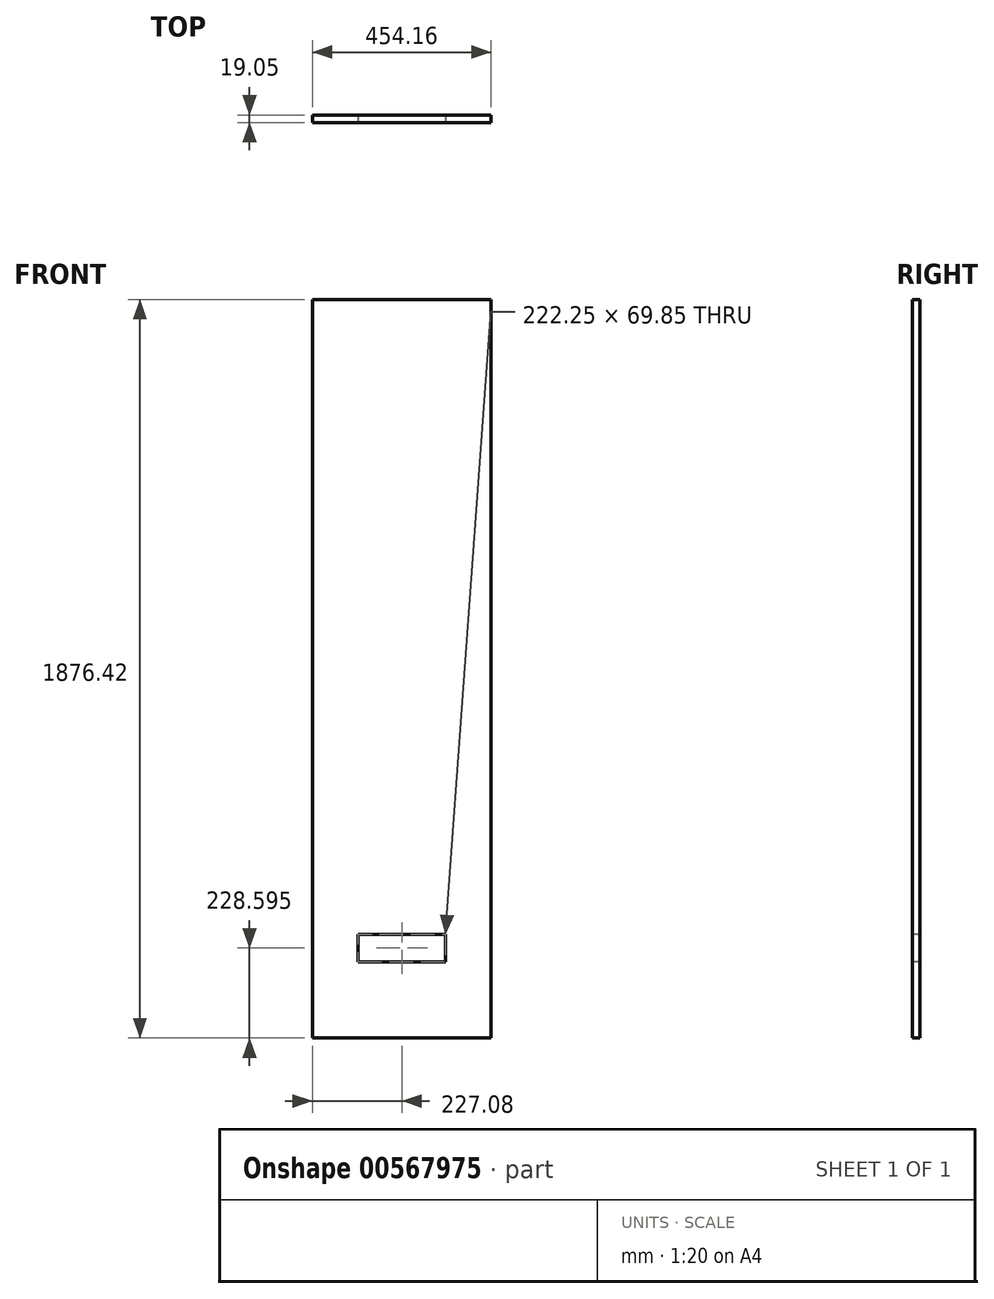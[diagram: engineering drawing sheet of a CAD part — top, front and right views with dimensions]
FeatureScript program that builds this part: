
annotation { "Feature Type Name" : "Feature", "Feature Type Description" : "" }
export const myFeature = defineFeature(function(context is Context, id is Id, definition is map)
    precondition{}
    {
        {
            var Q0;
            Q0=qCreatedBy(makeId("Front.planeOp"),FACE);
            var sketch = newSketch(context, id + "F0", { "sketchPlane" : qUnion([Q0])});
            skLineSegment(sketch, "E0.bottom", {"start": v(227.08, 965.2) * mm, "end": v(-227.08, 965.2) * mm});
            skLineSegment(sketch, "E0.top", {"start": v(227.08, -965.2) * mm, "end": v(-227.08, -965.2) * mm});
            skLineSegment(sketch, "E0.left", {"start": v(227.08, 965.2) * mm, "end": v(227.08, -965.2) * mm});
            skLineSegment(sketch, "E0.right", {"start": v(-227.08, 965.2) * mm, "end": v(-227.08, -965.2) * mm});
            skPoint(sketch, "E0.middle", {"position": v(0, 0) * mm});
            skSolve(sketch);
        }
        {
            var Q0;
            Q0=makeQuery(id+"F0.imprint","IMPRINT",FACE,{"disambiguationData":[TD([[makeQuery(id+"F0.imprint","IMPRINT",EDGE,{"derivedFrom":sQuery(id+"F0.wireOp",EDGE,"E0.bottom")}),1.0]])]});
            extrude(context, id + "F1", {"entities" : qUnion([Q0]), "depth" : 19.05 * mm, "offsetDistance" : 25.4 * mm});
        }
        {
            var Q0;
            Q0=makeQuery(id+"F1.opExtrude","SWEPT_FACE",FACE,{"disambiguationData":[OSD([sQuery(id+"F0.wireOp",EDGE,"E0.top")])]});
            extrude(context, id + "F2", {"entities" : qUnion([Q0]), "operationType" : NewBodyOperationType.REMOVE, "oppositeDirection" : true, "depth" : 53.97 * mm, "offsetDistance" : 25.4 * mm});
        }
        {
            var Q0;
            Q0=makeQuery(id+"F1.opExtrude","CAP_FACE",FACE,{"disambiguationData":[OSD([sQuery(id+"F0.wireOp",EDGE,"E0.bottom"),sQuery(id+"F0.wireOp",EDGE,"E0.top"),sQuery(id+"F0.wireOp",EDGE,"E0.left"),sQuery(id+"F0.wireOp",EDGE,"E0.right")])],"isStart":false});
            var sketch = newSketch(context, id + "F3", { "sketchPlane" : qUnion([Q0])});
            skLineSegment(sketch, "E1", {"start": v(0, -911.22) * mm, "end": v(0, -682.62) * mm});
            skLineSegment(sketch, "E2.bottom", {"start": v(111.13, -647.7) * mm, "end": v(-111.12, -647.7) * mm});
            skLineSegment(sketch, "E2.top", {"start": v(111.13, -717.55) * mm, "end": v(-111.13, -717.55) * mm});
            skLineSegment(sketch, "E2.left", {"start": v(111.13, -647.7) * mm, "end": v(111.13, -717.55) * mm});
            skLineSegment(sketch, "E2.right", {"start": v(-111.12, -647.7) * mm, "end": v(-111.13, -717.55) * mm});
            skPoint(sketch, "E2.middle", {"position": v(0, -682.62) * mm});
            skSolve(sketch);
        }
        {
            var Q0;
            Q0=makeQuery(id+"F3.imprint","IMPRINT",FACE,{"disambiguationData":[TD([[makeQuery(id+"F3.imprint","IMPRINT",EDGE,{"derivedFrom":sQuery(id+"F3.wireOp",EDGE,"E2.bottom")}),1.0]])]});
            extrude(context, id + "F4", {"entities" : qUnion([Q0]), "operationType" : NewBodyOperationType.REMOVE, "oppositeDirection" : true, "depth" : 25.4 * mm, "offsetDistance" : 25.4 * mm});
        }
    });
